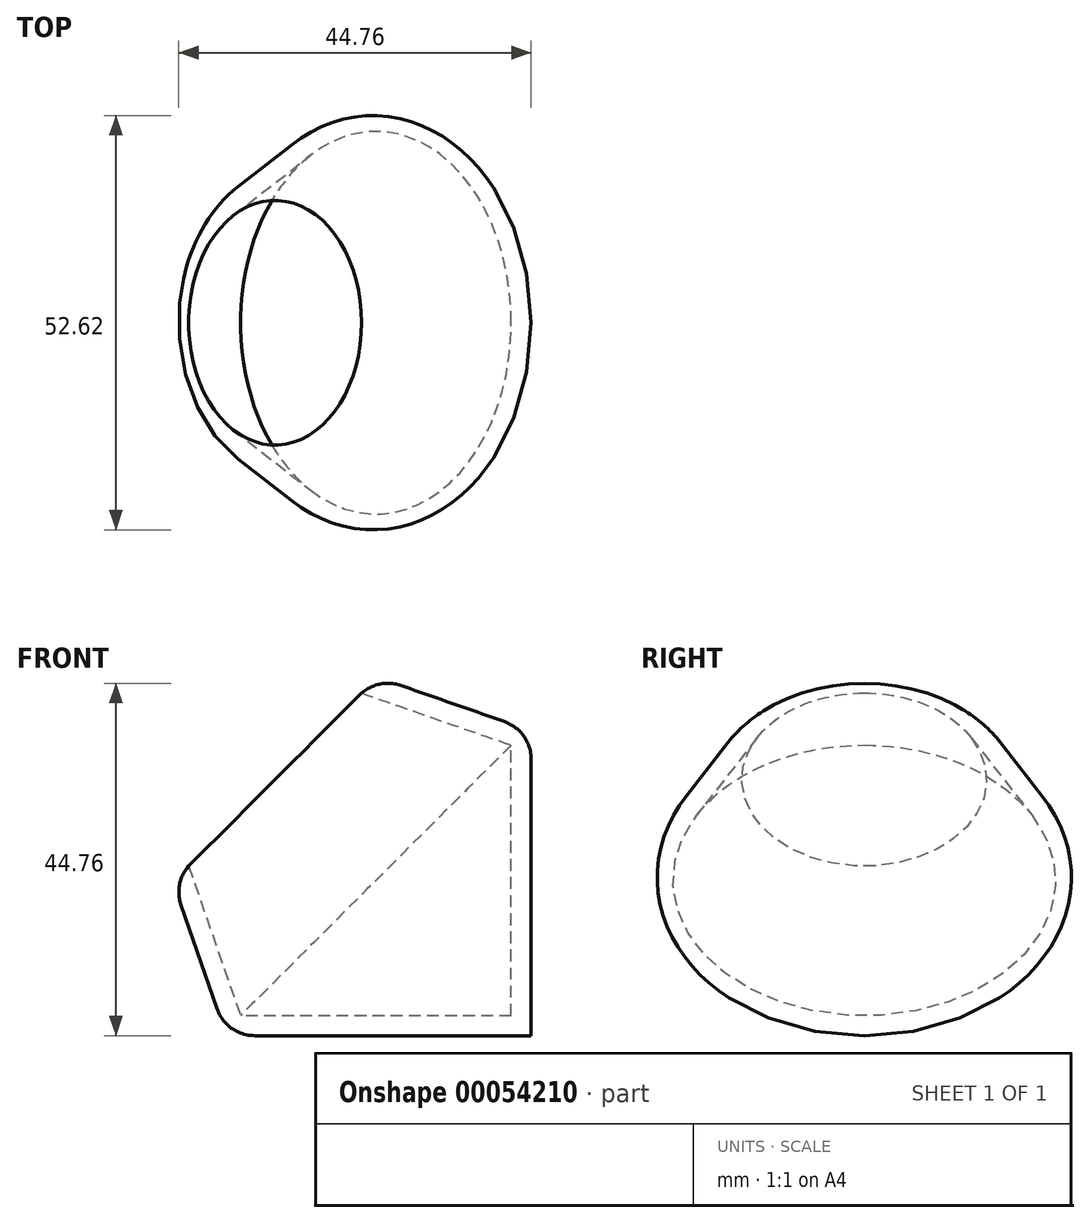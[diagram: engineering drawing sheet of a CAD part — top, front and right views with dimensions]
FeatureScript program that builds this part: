
annotation { "Feature Type Name" : "Feature", "Feature Type Description" : "" }
export const myFeature = defineFeature(function(context is Context, id is Id, definition is map)
    precondition{}
    {
        {
            var Q0;
            Q0=qCreatedBy(makeId("Front.planeOp"),FACE);
            var sketch = newSketch(context, id + "F0", { "sketchPlane" : qUnion([Q0])});
            skLineSegment(sketch, "E0", {"start": v(0, 0) * mm, "end": v(-38.71, 0) * mm});
            skLineSegment(sketch, "E1", {"start": v(-38.71, 0) * mm, "end": v(-45.37, 19.1) * mm});
            skLineSegment(sketch, "E2", {"start": v(-45.37, 19.1) * mm, "end": v(-34.09, 34.09) * mm});
            skLineSegment(sketch, "E3", {"start": v(-34.09, 34.09) * mm, "end": v(0, 0) * mm});
            skSolve(sketch);
        }
        {
            var Q0;
            Q0 = qSketchRegion(id + "F0", true);
            var Q1;
            Q1=sQuery(id+"F0.wireOp",EDGE,"E3");
            revolve(context, id + "F1", {"entities" : qUnion([Q0]), "axis" : qUnion([Q1]), "revolveType" : RevolveType.FULL});
        }
        {
            var Q0;
            Q0=makeQuery(id+"F1.opRevolve","SWEPT_FACE",FACE,{"disambiguationData":[OSD([sQuery(id+"F0.wireOp",EDGE,"E2")])]});
            shell(context, id + "F2", {"entities" : qUnion([Q0]), "thickness" : 2.54 * mm});
        }
        {
            var Q0;
            Q0=makeQuery(id+"F1.opRevolve","SWEPT_EDGE",EDGE,{"disambiguationData":[OSD([sQuery(id+"F0.wireOp",EDGE,"E1"),sQuery(id+"F0.wireOp",EDGE,"E2")])]});
            fillet(context, id + "F3", {"entities" : qUnion([Q0]), "radius" : 5.08 * mm, "tangentPropagation" : true, "allowEdgeOverflow" : false});
        }
        {
            var Q0;
            Q0=makeQuery(id+"F1.opRevolve","SWEPT_EDGE",EDGE,{"disambiguationData":[OSD([sQuery(id+"F0.wireOp",EDGE,"E0"),sQuery(id+"F0.wireOp",EDGE,"E1")])]});
            fillet(context, id + "F4", {"entities" : qUnion([Q0]), "radius" : 5.08 * mm, "tangentPropagation" : true, "allowEdgeOverflow" : false});
        }
    });
